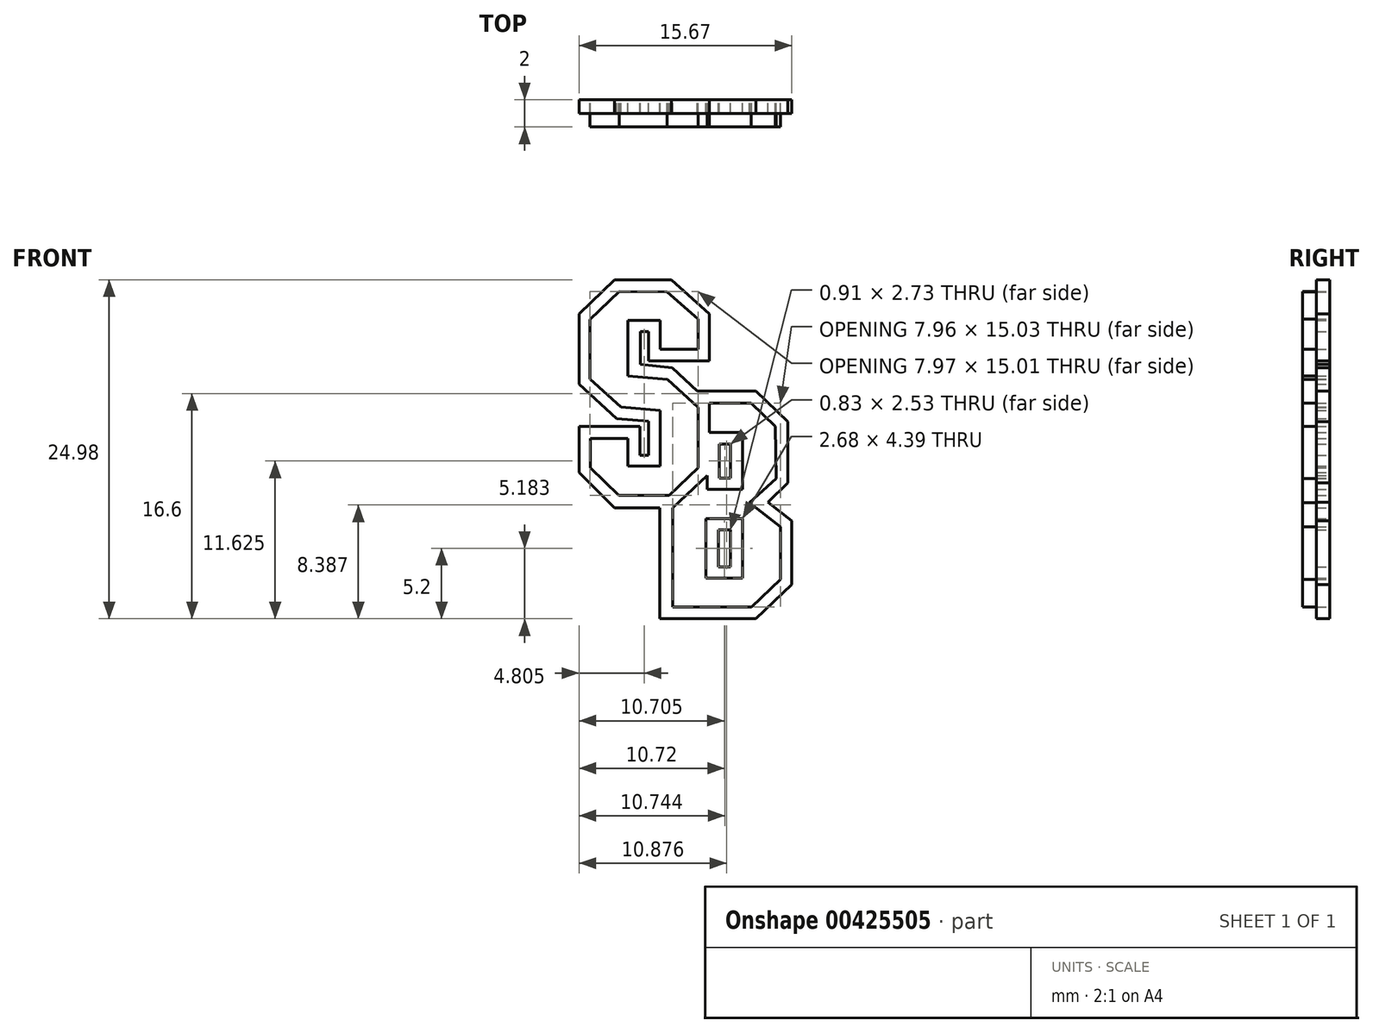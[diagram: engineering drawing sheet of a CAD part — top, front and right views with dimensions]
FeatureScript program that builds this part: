
annotation { "Feature Type Name" : "Feature", "Feature Type Description" : "" }
export const myFeature = defineFeature(function(context is Context, id is Id, definition is map)
    precondition{}
    {
        {
            var Q0;
            Q0=qCreatedBy(makeId("Front.planeOp"),FACE);
            var sketch = newSketch(context, id + "F0", { "sketchPlane" : qUnion([Q0])});
            skLineSegment(sketch, "E0", {"start": v(-9.97, 5.95) * mm, "end": v(-12.6, 3.42) * mm});
            skLineSegment(sketch, "E1", {"start": v(-12.6, 3.42) * mm, "end": v(-12.6, -1.74) * mm});
            skLineSegment(sketch, "E2", {"start": v(-12.6, -1.74) * mm, "end": v(-9.8, -4.3) * mm});
            skLineSegment(sketch, "E3", {"start": v(-9.8, -4.3) * mm, "end": v(-7.48, -4.47) * mm});
            skLineSegment(sketch, "E4", {"start": v(-7.48, -4.47) * mm, "end": v(-7.48, -6.97) * mm});
            skLineSegment(sketch, "E5", {"start": v(-7.48, -6.97) * mm, "end": v(-8.1, -6.97) * mm});
            skLineSegment(sketch, "E6", {"start": v(-8.1, -6.97) * mm, "end": v(-8.1, -4.86) * mm});
            skLineSegment(sketch, "E7", {"start": v(-8.1, -4.86) * mm, "end": v(-12.6, -4.86) * mm});
            skLineSegment(sketch, "E8", {"start": v(-12.6, -4.86) * mm, "end": v(-12.6, -8.25) * mm});
            skLineSegment(sketch, "E9", {"start": v(-12.6, -8.25) * mm, "end": v(-9.97, -10.85) * mm});
            skLineSegment(sketch, "E10", {"start": v(-9.97, -10.85) * mm, "end": v(-5.69, -10.85) * mm});
            skLineSegment(sketch, "E11", {"start": v(-5.69, -10.85) * mm, "end": v(-2.98, -8.31) * mm});
            skLineSegment(sketch, "E12", {"start": v(-2.98, -8.31) * mm, "end": v(-2.98, -3.13) * mm});
            skLineSegment(sketch, "E13", {"start": v(-2.98, -3.13) * mm, "end": v(-5.71, -0.53) * mm});
            skLineSegment(sketch, "E14", {"start": v(-5.71, -0.53) * mm, "end": v(-8.07, -0.3) * mm});
            skLineSegment(sketch, "E15", {"start": v(-8.07, -0.3) * mm, "end": v(-8.07, 2.11) * mm});
            skLineSegment(sketch, "E16", {"start": v(-8.07, 2.11) * mm, "end": v(-7.48, 2.11) * mm});
            skLineSegment(sketch, "E17", {"start": v(-7.48, 2.11) * mm, "end": v(-7.48, -0.03) * mm});
            skLineSegment(sketch, "E18", {"start": v(-7.48, -0.03) * mm, "end": v(-2.98, -0.03) * mm});
            skLineSegment(sketch, "E19", {"start": v(-2.98, -0.03) * mm, "end": v(-2.98, 3.42) * mm});
            skLineSegment(sketch, "E20", {"start": v(-2.98, 3.42) * mm, "end": v(-5.78, 5.95) * mm});
            skLineSegment(sketch, "E21", {"start": v(-5.78, 5.95) * mm, "end": v(-9.97, 5.95) * mm});
            skLineSegment(sketch, "E22", {"start": v(-9.65, 5.08) * mm, "end": v(-11.78, 3.02) * mm});
            skLineSegment(sketch, "E23", {"start": v(-11.78, 3.02) * mm, "end": v(-11.78, -1.37) * mm});
            skLineSegment(sketch, "E24", {"start": v(-11.78, -1.37) * mm, "end": v(-9.52, -3.43) * mm});
            skLineSegment(sketch, "E25", {"start": v(-9.52, -3.43) * mm, "end": v(-6.61, -3.68) * mm});
            skLineSegment(sketch, "E26", {"start": v(-6.61, -3.68) * mm, "end": v(-6.61, -7.78) * mm});
            skLineSegment(sketch, "E27", {"start": v(-6.61, -7.78) * mm, "end": v(-9, -7.78) * mm});
            skLineSegment(sketch, "E28", {"start": v(-9, -7.78) * mm, "end": v(-9, -5.75) * mm});
            skLineSegment(sketch, "E29", {"start": v(-9, -5.75) * mm, "end": v(-11.74, -5.75) * mm});
            skLineSegment(sketch, "E30", {"start": v(-11.74, -5.75) * mm, "end": v(-11.74, -7.9) * mm});
            skLineSegment(sketch, "E31", {"start": v(-11.74, -7.9) * mm, "end": v(-9.66, -9.94) * mm});
            skLineSegment(sketch, "E32", {"start": v(-9.66, -9.94) * mm, "end": v(-5.95, -9.94) * mm});
            skLineSegment(sketch, "E33", {"start": v(-5.95, -9.94) * mm, "end": v(-3.81, -7.9) * mm});
            skLineSegment(sketch, "E34", {"start": v(-3.81, -7.9) * mm, "end": v(-3.81, -3.46) * mm});
            skLineSegment(sketch, "E35", {"start": v(-3.81, -3.46) * mm, "end": v(-6.08, -1.4) * mm});
            skLineSegment(sketch, "E36", {"start": v(-6.08, -1.4) * mm, "end": v(-9, -1.13) * mm});
            skLineSegment(sketch, "E37", {"start": v(-9, -1.13) * mm, "end": v(-9, 2.97) * mm});
            skLineSegment(sketch, "E38", {"start": v(-9, 2.97) * mm, "end": v(-6.62, 2.97) * mm});
            skLineSegment(sketch, "E39", {"start": v(-6.62, 2.97) * mm, "end": v(-6.62, 0.82) * mm});
            skLineSegment(sketch, "E40", {"start": v(-6.62, 0.82) * mm, "end": v(-3.81, 0.82) * mm});
            skLineSegment(sketch, "E41", {"start": v(-3.81, 0.82) * mm, "end": v(-3.81, 3.06) * mm});
            skLineSegment(sketch, "E42", {"start": v(-3.81, 3.06) * mm, "end": v(-6.12, 5.05) * mm});
            skLineSegment(sketch, "E43", {"start": v(-6.12, 5.05) * mm, "end": v(-9.65, 5.08) * mm});
            skLineSegment(sketch, "E44", {"start": v(-3.89, -2.27) * mm, "end": v(0.43, -2.27) * mm});
            skLineSegment(sketch, "E45", {"start": v(0.43, -2.27) * mm, "end": v(2.78, -4.5) * mm});
            skLineSegment(sketch, "E46", {"start": v(2.78, -4.5) * mm, "end": v(2.78, -9.03) * mm});
            skLineSegment(sketch, "E47", {"start": v(2.78, -9.03) * mm, "end": v(1.32, -10.46) * mm});
            skLineSegment(sketch, "E48", {"start": v(1.32, -10.46) * mm, "end": v(3.07, -11.82) * mm});
            skLineSegment(sketch, "E49", {"start": v(3.07, -11.82) * mm, "end": v(3.07, -16.5) * mm});
            skLineSegment(sketch, "E50", {"start": v(3.07, -16.5) * mm, "end": v(0.45, -19.03) * mm});
            skLineSegment(sketch, "E51", {"start": v(0.45, -19.03) * mm, "end": v(-6.63, -19.03) * mm});
            skLineSegment(sketch, "E52", {"start": v(-6.63, -19.03) * mm, "end": v(-6.63, -10.85) * mm});
            skLineSegment(sketch, "E53", {"start": v(-2.98, -3.13) * mm, "end": v(0.08, -3.13) * mm});
            skLineSegment(sketch, "E54", {"start": v(0.08, -3.13) * mm, "end": v(1.86, -4.87) * mm});
            skLineSegment(sketch, "E55", {"start": v(1.86, -4.87) * mm, "end": v(1.91, -8.7) * mm});
            skLineSegment(sketch, "E56", {"start": v(1.91, -8.7) * mm, "end": v(-0.04, -10.48) * mm});
            skLineSegment(sketch, "E57", {"start": v(-0.04, -10.48) * mm, "end": v(2.26, -12.27) * mm});
            skLineSegment(sketch, "E58", {"start": v(2.26, -12.27) * mm, "end": v(2.26, -16.12) * mm});
            skLineSegment(sketch, "E59", {"start": v(2.26, -16.12) * mm, "end": v(0.12, -18.16) * mm});
            skLineSegment(sketch, "E60", {"start": v(0.12, -18.16) * mm, "end": v(-5.7, -18.16) * mm});
            skLineSegment(sketch, "E61", {"start": v(-5.7, -18.16) * mm, "end": v(-5.69, -10.85) * mm});
            skLineSegment(sketch, "E62", {"start": v(-3.15, -8.47) * mm, "end": v(-3.15, -9.5) * mm});
            skLineSegment(sketch, "E63", {"start": v(-3.15, -9.5) * mm, "end": v(-0.55, -9.5) * mm});
            skLineSegment(sketch, "E64", {"start": v(-0.55, -9.5) * mm, "end": v(-0.55, -5.3) * mm});
            skLineSegment(sketch, "E65", {"start": v(-0.55, -5.3) * mm, "end": v(-2.98, -5.3) * mm});
            skLineSegment(sketch, "E66", {"start": v(-2.27, -6.14) * mm, "end": v(-2.27, -8.67) * mm});
            skLineSegment(sketch, "E67", {"start": v(-2.27, -8.67) * mm, "end": v(-1.44, -8.67) * mm});
            skLineSegment(sketch, "E68", {"start": v(-1.44, -8.67) * mm, "end": v(-1.44, -6.14) * mm});
            skLineSegment(sketch, "E69", {"start": v(-2.27, -6.14) * mm, "end": v(-1.44, -6.14) * mm});
            skLineSegment(sketch, "E70", {"start": v(-3.2, -11.63) * mm, "end": v(-0.55, -11.63) * mm});
            skLineSegment(sketch, "E71", {"start": v(-0.55, -11.63) * mm, "end": v(-0.55, -16.02) * mm});
            skLineSegment(sketch, "E72", {"start": v(-0.55, -16.02) * mm, "end": v(-3.24, -16.02) * mm});
            skLineSegment(sketch, "E73", {"start": v(-3.24, -16.02) * mm, "end": v(-3.24, -11.63) * mm});
            skLineSegment(sketch, "E74", {"start": v(-3.24, -11.63) * mm, "end": v(-3.19, -11.63) * mm});
            skLineSegment(sketch, "E75", {"start": v(-2.34, -12.48) * mm, "end": v(-1.42, -12.48) * mm});
            skLineSegment(sketch, "E76", {"start": v(-1.42, -12.48) * mm, "end": v(-1.42, -15.21) * mm});
            skLineSegment(sketch, "E77", {"start": v(-1.42, -15.21) * mm, "end": v(-2.32, -15.21) * mm});
            skLineSegment(sketch, "E78", {"start": v(-2.32, -15.21) * mm, "end": v(-2.34, -12.48) * mm});
            skSolve(sketch);
        }
        {
            var Q0;
            Q0=makeQuery(id+"F0.imprint","IMPRINT",FACE,{"disambiguationData":[TD([[makeQuery(id+"F0.imprint","IMPRINT",EDGE,{"derivedFrom":sQuery(id+"F0.wireOp",EDGE,"E22")}),1.0]])]});
            var Q1;
            {var subQ0=sQuery(id+"F0.wireOp",EDGE,"E53");Q1=makeQuery(id+"F0.imprint","IMPRINT",FACE,{"disambiguationData":[TD([[makeQuery(id+"F0.imprint","IMPRINT",EDGE,{"derivedFrom":subQ0}),-1.0]])]});}
            extrude(context, id + "F1", {"entities" : qUnion([Q0, Q1]), "depth" : 2 * mm});
        }
        {
            var Q0;
            Q0=makeQuery(id+"F0.imprint","IMPRINT",FACE,{"disambiguationData":[TD([[makeQuery(id+"F0.imprint","IMPRINT",EDGE,{"derivedFrom":sQuery(id+"F0.wireOp",EDGE,"E0")}),1.0]])]});
            var Q1;
            {var subQ0=sQuery(id+"F0.wireOp",EDGE,"E62");Q1=makeQuery(id+"F0.imprint","IMPRINT",FACE,{"disambiguationData":[TD([[makeQuery(id+"F0.imprint","IMPRINT",EDGE,{"derivedFrom":subQ0}),1.0]])]});}
            var Q2;
            {var subQ1=sQuery(id+"F0.wireOp",EDGE,"E70");Q2=makeQuery(id+"F0.imprint","IMPRINT",FACE,{"disambiguationData":[TD([[makeQuery(id+"F0.imprint","IMPRINT",EDGE,{"derivedFrom":subQ1}),-1.0]])]});}
            var Q3;
            {var subQ4=sQuery(id+"F0.wireOp",EDGE,"E44");Q3=makeQuery(id+"F0.imprint","IMPRINT",FACE,{"disambiguationData":[TD([[makeQuery(id+"F0.imprint","IMPRINT",EDGE,{"derivedFrom":subQ4}),-1.0]])]});}
            extrude(context, id + "F2", {"entities" : qUnion([Q0, Q1, Q2, Q3]), "depth" : 1 * mm});
        }
    });
